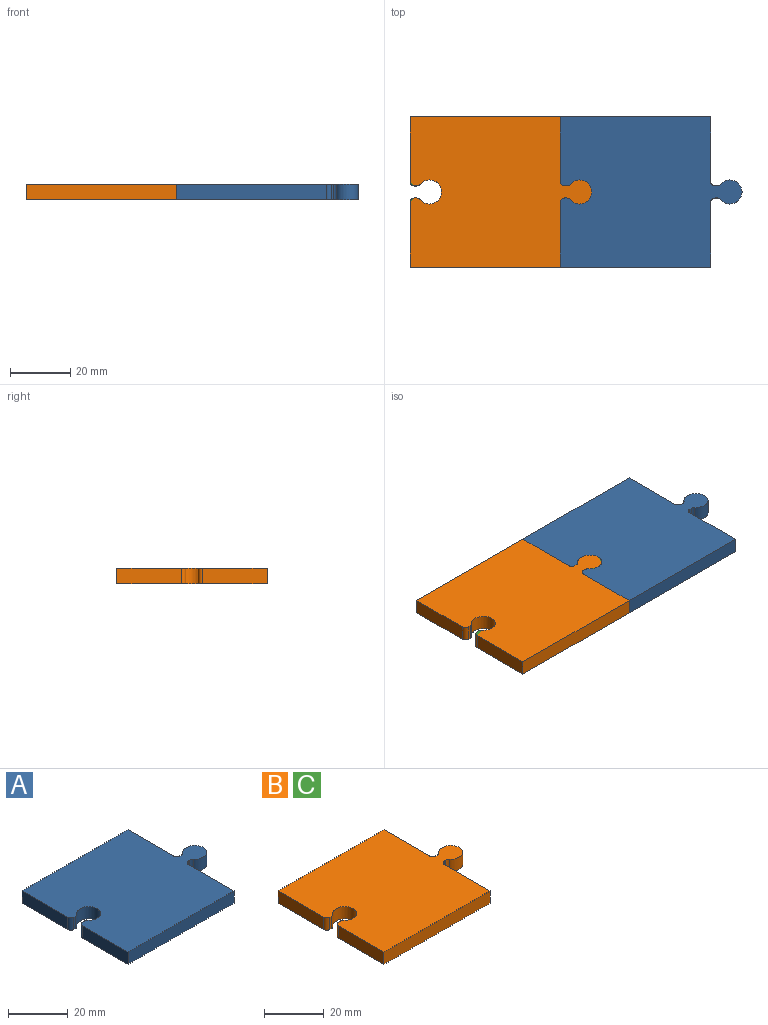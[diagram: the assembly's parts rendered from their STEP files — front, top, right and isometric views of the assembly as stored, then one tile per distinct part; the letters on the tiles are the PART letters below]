
ASSEMBLY  parts=3 mates=1
PART A: 22 faces, bbox 60.5x50x5 mm
  f0: cylinder r=1.5mm len=5mm, axis (0,0,-1), area 11.8mm2, adj f1,f19,f20,f21
  f1: plane 21.5x5mm, normal (1,0,0), area 107.5mm2, adj f0,f2,f20,f21
  f2: plane 50x5mm, normal (0,1,0), area 250mm2, adj f1,f3,f20,f21
  f3: plane 21.5x5mm, normal (-1,0,0), area 107.5mm2, adj f2,f4,f20,f21
  f4: cylinder r=1.5mm len=5mm, axis (0,0,-1), area 11.8mm2, adj f3,f5,f20,f21
  f5: plane 5x0.72mm, normal (0,-1,0), area 3.6mm2, adj f4,f6,f20,f21
  f6: cylinder r=1.5mm len=5mm, axis (0,0,-1), area 6.6mm2, adj f5,f7,f20,f21
  f7: cylinder r=4mm len=8mm, axis (0,0,-1), area 98.1mm2, adj f6,f8,f20,f21
  f8: cylinder r=1.5mm len=5mm, axis (0,0,-1), area 6.6mm2, adj f7,f9,f20,f21
  f9: plane 5x0.72mm, normal (0,1,0), area 3.6mm2, adj f8,f10,f20,f21
  f10: cylinder r=1.5mm len=5mm, axis (0,0,-1), area 11.8mm2, adj f9,f11,f20,f21
  f11: plane 21.5x5mm, normal (-1,0,0), area 107.5mm2, adj f10,f12,f20,f21
  f12: plane 50x5mm, normal (0,-1,0), area 250mm2, adj f11,f13,f20,f21
  f13: plane 21.5x5mm, normal (1,0,0), area 107.5mm2, adj f12,f14,f20,f21
  f14: cylinder r=1.5mm len=5mm, axis (0,0,-1), area 11.8mm2, adj f13,f15,f20,f21
  f15: plane 5x0.72mm, normal (0,-1,0), area 3.6mm2, adj f14,f16,f20,f21
  f16: cylinder r=1.5mm len=5mm, axis (0,0,-1), area 6.6mm2, adj f15,f17,f20,f21
  f17: cylinder r=4mm len=8mm, axis (0,0,-1), area 98.1mm2, adj f16,f18,f20,f21
  f18: cylinder r=1.5mm len=5mm, axis (0,0,-1), area 6.6mm2, adj f17,f19,f20,f21
  f19: plane 5x0.72mm, normal (0,1,0), area 3.6mm2, adj f0,f18,f20,f21
  f20: plane 60.46x50mm, normal (0,0,1), area 2500mm2, adj f0,f1,f2,f3,f4,f5,f6,f7
  f21: plane 60.46x50mm, normal (0,0,-1), area 2500mm2, adj f0,f1,f2,f3,f4,f5,f6,f7
PART B: 22 faces, bbox 60.5x50x5 mm
  f0: cylinder r=1.5mm len=5mm, axis (0,0,-1), area 6.6mm2, adj f1,f19,f20,f21
  f1: cylinder r=4mm len=8mm, axis (0,0,-1), area 98.1mm2, adj f0,f2,f20,f21
  f2: cylinder r=1.5mm len=5mm, axis (0,0,-1), area 6.6mm2, adj f1,f3,f20,f21
  f3: plane 5x0.72mm, normal (0,1,0), area 3.6mm2, adj f2,f4,f20,f21
  f4: cylinder r=1.5mm len=5mm, axis (0,0,-1), area 11.8mm2, adj f3,f5,f20,f21
  f5: plane 21.5x5mm, normal (1,0,0), area 107.5mm2, adj f4,f6,f20,f21
  f6: plane 50x5mm, normal (0,1,0), area 250mm2, adj f5,f7,f20,f21
  f7: plane 21.5x5mm, normal (-1,0,0), area 107.5mm2, adj f6,f8,f20,f21
  f8: cylinder r=1.5mm len=5mm, axis (0,0,-1), area 11.8mm2, adj f7,f9,f20,f21
  f9: plane 5x0.72mm, normal (0,-1,0), area 3.6mm2, adj f8,f10,f20,f21
  f10: cylinder r=1.5mm len=5mm, axis (0,0,-1), area 6.6mm2, adj f9,f11,f20,f21
  f11: cylinder r=4mm len=8mm, axis (0,0,-1), area 98.1mm2, adj f10,f12,f20,f21
  f12: cylinder r=1.5mm len=5mm, axis (0,0,-1), area 6.6mm2, adj f11,f13,f20,f21
  f13: plane 5x0.72mm, normal (0,1,0), area 3.6mm2, adj f12,f14,f20,f21
  f14: cylinder r=1.5mm len=5mm, axis (0,0,-1), area 11.8mm2, adj f13,f15,f20,f21
  f15: plane 21.5x5mm, normal (-1,0,0), area 107.5mm2, adj f14,f16,f20,f21
  f16: plane 50x5mm, normal (0,-1,0), area 250mm2, adj f15,f17,f20,f21
  f17: plane 21.5x5mm, normal (1,0,0), area 107.5mm2, adj f16,f18,f20,f21
  f18: cylinder r=1.5mm len=5mm, axis (0,0,-1), area 11.8mm2, adj f17,f19,f20,f21
  f19: plane 5x0.72mm, normal (0,-1,0), area 3.6mm2, adj f0,f18,f20,f21
  f20: plane 60.46x50mm, normal (0,0,1), area 2500mm2, adj f0,f1,f2,f3,f4,f5,f6,f7
  f21: plane 60.46x50mm, normal (0,0,-1), area 2500mm2, adj f0,f1,f2,f3,f4,f5,f6,f7
PART C: same geometry as B
PLACE A t=(23.91,13.45,-1.14)mm
PLACE B t=(-12.98,5.38,-1.14)mm
PLACE C t=(-12.98,5.38,-1.14)mm
MATE fastened A.f7 <-> B.f1  axis (0,0,-1) through (15.18,10.17,-1.14)mm
